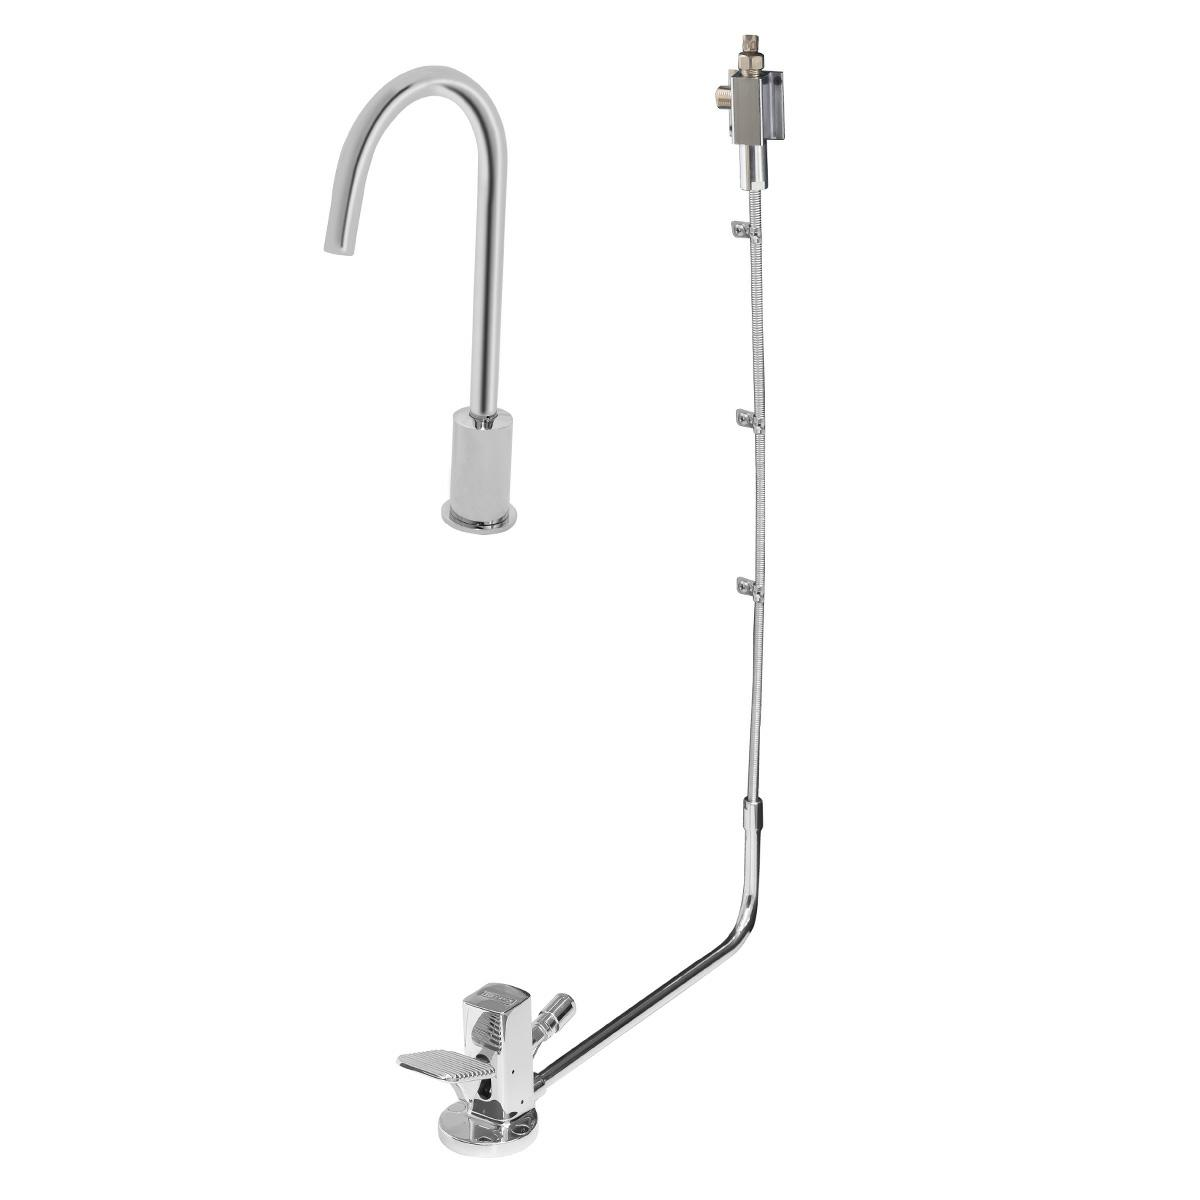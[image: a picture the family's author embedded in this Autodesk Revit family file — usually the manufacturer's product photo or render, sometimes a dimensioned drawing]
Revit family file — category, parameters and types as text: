
# Revit family: VP-2_RFA
name_source: partatom
category: Aparatos sanitarios
units: mm (PartAtom-declared; Revit-internal decimal feet)

## family parameters
Compartido = Sí
Corte con vacíos al cargar = No
Cota de conector redondo = Diámetro de uso
Número OmniClass = 23.45.55.14
Punto de cálculo de habitación = Sí
Se basa en plano de trabajo = Sí
Siempre vertical = Sí
Tipo de pieza = Normal
Título OmniClass = Single Faucets

## types (1)
- VP-2
    Accesorios = Conectores ½ -14 NPSM
    Características del Producto = Llave para lavabo con pedal expuesto, sin contra
    Comentarios de tipo = Monomando para lavabo.
    Cuerpo de Latón = Brass
    Descripción = Llave para lavabo con pedal expuesto
    Elevación por defecto = 1"
    Fabricante = HELVEX S.A. de C.V.
    Garantía = El producto HELVEX está garantizado como libre de defectos en materiales y procesos de fabricación. El producto HELVEX está garantizado, en lo que se refiere a los acabados; por un periodo de 10 años en los acabados cromo y duravex, y por 2 años en acabados diferentes al cromo, a partir de la fecha de compra indicada en la factura
    Hoja Técnica = https://www.helvex.com.mx
    Imagen de tipo = VP-2.jpg
    Instalación = Conexión ½ - 14 NPSM
    Instructivo = https://www.helvex.com.mx
    Modelo = VP-2
    Operación = Para abrir el flujo de agua oprima el pedal con el pie.
    Presión Máxima de Trabajo = 85.3 psi
    Presión Mínima de Trabajo = 3.6 psi
    Total Height = 14"
    Total Lenght = 8"
    Total Width = 2"
    URL = https://www.helvex.com.mx

## geometry (parser evidence)
native form markers: Sweep x3
no freeform markers — native parametric forms only
